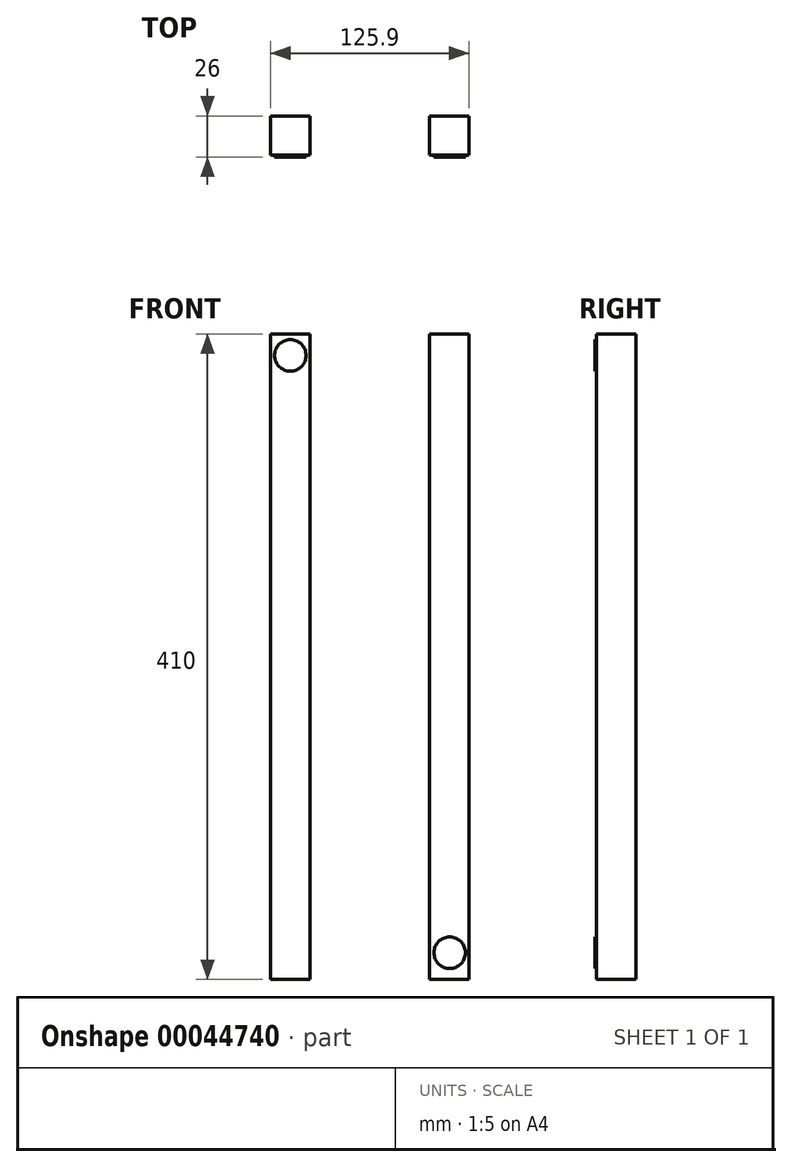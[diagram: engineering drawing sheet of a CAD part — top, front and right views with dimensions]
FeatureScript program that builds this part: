
annotation { "Feature Type Name" : "Feature", "Feature Type Description" : "" }
export const myFeature = defineFeature(function(context is Context, id is Id, definition is map)
    precondition{}
    {
        {
            var Q0;
            Q0=qCreatedBy(makeId("Top.planeOp"),FACE);
            var sketch = newSketch(context, id + "F0", { "sketchPlane" : qUnion([Q0])});
            skLineSegment(sketch, "E0.bottom", {"start": v(21.3, 15.32) * mm, "end": v(46.3, 15.32) * mm});
            skLineSegment(sketch, "E0.top", {"start": v(21.3, -9.68) * mm, "end": v(46.3, -9.68) * mm});
            skLineSegment(sketch, "E0.left", {"start": v(21.3, 15.32) * mm, "end": v(21.3, -9.68) * mm});
            skLineSegment(sketch, "E0.right", {"start": v(46.3, 15.32) * mm, "end": v(46.3, -9.68) * mm});
            skLineSegment(sketch, "E1.bottom", {"start": v(-54.6, 15.32) * mm, "end": v(-79.6, 15.32) * mm});
            skLineSegment(sketch, "E1.top", {"start": v(-54.6, -9.68) * mm, "end": v(-79.6, -9.68) * mm});
            skLineSegment(sketch, "E1.left", {"start": v(-54.6, 15.32) * mm, "end": v(-54.6, -9.68) * mm});
            skLineSegment(sketch, "E1.right", {"start": v(-79.6, 15.32) * mm, "end": v(-79.6, -9.68) * mm});
            skLineSegment(sketch, "E2", {"start": v(-77.03, -9.68) * mm, "end": v(111.02, -9.68) * mm, "construction": true});
            skPoint(sketch, "E2.endSnap0", {"position": v(33.8, -9.68) * mm});
            skSolve(sketch);
        }
        {
            var Q0;
            Q0=makeQuery(id+"F0.imprint","IMPRINT",FACE,{"disambiguationData":[TD([[makeQuery(id+"F0.imprint","IMPRINT",EDGE,{"derivedFrom":sQuery(id+"F0.wireOp",EDGE,"E1.bottom")}),1.0]])]});
            var Q1;
            Q1=makeQuery(id+"F0.imprint","IMPRINT",FACE,{"disambiguationData":[TD([[makeQuery(id+"F0.imprint","IMPRINT",EDGE,{"derivedFrom":sQuery(id+"F0.wireOp",EDGE,"E0.bottom")}),-1.0]])]});
            extrude(context, id + "F1", {"entities" : qUnion([Q0, Q1]), "depth" : 410 * mm});
        }
        {
            var Q0;
            Q0=makeQuery(id+"F1.opExtrude","SWEPT_FACE",FACE,{"disambiguationData":[OSD([sQuery(id+"F0.wireOp",EDGE,"E1.top")])]});
            var sketch = newSketch(context, id + "F2", { "sketchPlane" : qUnion([Q0])});
            skCircle(sketch, "E3", {"center": v(-67.1, 396.41) * mm, "radius": 10 * mm});
            skPoint(sketch, "E3.centerSnap0", {"position": v(-67.1, 410) * mm});
            skCircle(sketch, "E4", {"center": v(34.15, 17.02) * mm, "radius": 10 * mm});
            skSolve(sketch);
        }
        {
            var Q0;
            Q0=makeQuery(id+"F2.imprint","IMPRINT",FACE,{"disambiguationData":[TD([[makeQuery(id+"F2.imprint","IMPRINT",EDGE,{"derivedFrom":sQuery(id+"F2.wireOp",EDGE,"E3")}),1.0]])]});
            extrude(context, id + "F3", {"entities" : qUnion([Q0]), "operationType" : NewBodyOperationType.ADD, "depth" : 1 * mm});
        }
        {
            var Q0;
            Q0=makeQuery(id+"F2.imprint","IMPRINT",FACE,{"disambiguationData":[TD([[makeQuery(id+"F2.imprint","IMPRINT",EDGE,{"derivedFrom":sQuery(id+"F2.wireOp",EDGE,"E4")}),1.0]])]});
            extrude(context, id + "F4", {"entities" : qUnion([Q0]), "operationType" : NewBodyOperationType.ADD, "depth" : 1 * mm});
        }
    });
